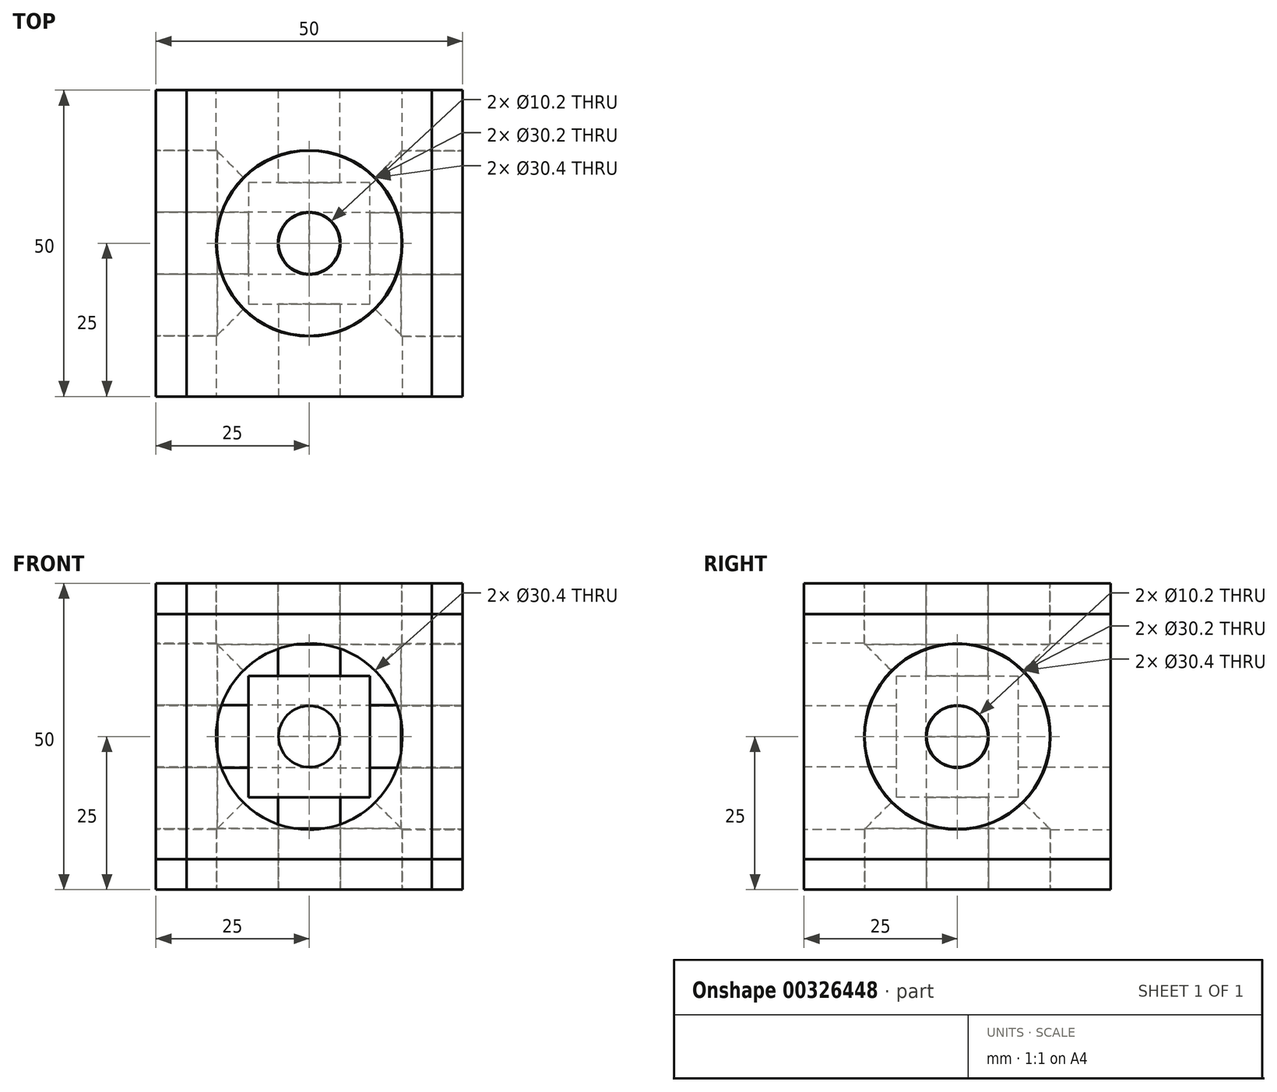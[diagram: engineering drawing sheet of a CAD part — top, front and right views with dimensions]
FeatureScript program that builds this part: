
annotation { "Feature Type Name" : "Feature", "Feature Type Description" : "" }
export const myFeature = defineFeature(function(context is Context, id is Id, definition is map)
    precondition{}
    {
        {
            var Q0;
            Q0=qCreatedBy(makeId("Top.planeOp"),FACE);
            var sketch = newSketch(context, id + "F0", { "sketchPlane" : qUnion([Q0])});
            skLineSegment(sketch, "E0.bottom", {"start": v(25, -25) * mm, "end": v(-25, -25) * mm});
            skLineSegment(sketch, "E0.top", {"start": v(25, 25) * mm, "end": v(-25, 25) * mm});
            skLineSegment(sketch, "E0.left", {"start": v(25, -25) * mm, "end": v(25, 25) * mm});
            skLineSegment(sketch, "E0.right", {"start": v(-25, -25) * mm, "end": v(-25, 25) * mm});
            skPoint(sketch, "E0.middle", {"position": v(0, 0) * mm});
            skSolve(sketch);
        }
        {
            var Q0;
            Q0 = qSketchRegion(id + "F0", true);
            extrude(context, id + "F1", {"entities" : qUnion([Q0]), "endBound" : BoundingType.SYMMETRIC, "depth" : 50 * mm});
        }
        {
            var Q0;
            Q0=makeQuery(id+"F1.opExtrude","CAP_FACE",FACE,{"disambiguationData":[OSD([sQuery(id+"F0.wireOp",EDGE,"E0.bottom"),sQuery(id+"F0.wireOp",EDGE,"E0.top"),sQuery(id+"F0.wireOp",EDGE,"E0.left"),sQuery(id+"F0.wireOp",EDGE,"E0.right")])],"isStart":false});
            var sketch = newSketch(context, id + "F2", { "sketchPlane" : qUnion([Q0])});
            skCircle(sketch, "E1", {"center": v(0, 0) * mm, "radius": 15.1 * mm});
            skCircle(sketch, "E2", {"center": v(0, 0) * mm, "radius": 5.1 * mm});
            skSolve(sketch);
        }
        {
            var Q0;
            Q0=qCreatedBy(makeId("Top.planeOp"),FACE);
            var sketch = newSketch(context, id + "F3", { "sketchPlane" : qUnion([Q0])});
            skPoint(sketch, "E3.0", {"position": v(0, 25) * mm});
            skPoint(sketch, "E4.0", {"position": v(0, -25) * mm});
            skLineSegment(sketch, "E5", {"start": v(0, 25) * mm, "end": v(0, -25) * mm, "construction": true});
            skPoint(sketch, "E6.0", {"position": v(-25, 0) * mm});
            skPoint(sketch, "E7.0", {"position": v(25, 0) * mm});
            skLineSegment(sketch, "E8", {"start": v(-25, 0) * mm, "end": v(25, 0) * mm, "construction": true});
            skSolve(sketch);
        }
        {
            var Q0;
            Q0=makeQuery(id+"F2.imprint","IMPRINT",FACE,{"disambiguationData":[TD([[makeQuery(id+"F2.imprint","IMPRINT",EDGE,{"derivedFrom":sQuery(id+"F2.wireOp",EDGE,"E2")}),1.0]])]});
            extrude(context, id + "F4", {"entities" : qUnion([Q0]), "oppositeDirection" : true, "depth" : 25 * mm});
        }
        {
            var Q0;
            Q0=makeQuery(id+"F2.imprint","IMPRINT",FACE,{"disambiguationData":[TD([[makeQuery(id+"F2.imprint","IMPRINT",EDGE,{"derivedFrom":sQuery(id+"F2.wireOp",EDGE,"E1")}),1.0]])]});
            extrude(context, id + "F5", {"entities" : qUnion([Q0]), "oppositeDirection" : true, "depth" : 15 * mm});
        }
        {
            var Q0;
            Q0=makeQuery(id+"F2.imprint","IMPRINT",FACE,{"disambiguationData":[TD([[makeQuery(id+"F2.imprint","IMPRINT",EDGE,{"derivedFrom":sQuery(id+"F2.wireOp",EDGE,"E1")}),1.0]])]});
            extrude(context, id + "F6", {"entities" : qUnion([Q0]), "oppositeDirection" : true, "depth" : 10 * mm});
        }
        {
            var Q0;
            Q0=makeQuery(id+"F2.imprint","IMPRINT",FACE,{"disambiguationData":[TD([[makeQuery(id+"F2.imprint","IMPRINT",EDGE,{"derivedFrom":sQuery(id+"F2.wireOp",EDGE,"E1")}),-1.0]])]});
            extrude(context, id + "F7", {"entities" : qUnion([Q0]), "oppositeDirection" : true, "depth" : 5 * mm});
        }
        {
            var Q0;
            Q0=makeQuery(id+"F4.opExtrude","SWEPT_BODY",BODY,{"disambiguationData":[OSD([sQuery(id+"F2.wireOp",EDGE,"E2")])]});
            var Q1;
            Q1=makeQuery(id+"F5.opExtrude","SWEPT_BODY",BODY,{"disambiguationData":[OSD([sQuery(id+"F2.wireOp",EDGE,"O8aLxC34-7BVB-v1Gc-gPhH-KugDPPAYjpQ1"),sQuery(id+"F2.wireOp",EDGE,"E2")])]});
            var Q2;
            Q2=makeQuery(id+"F6.opExtrude","SWEPT_BODY",BODY,{"disambiguationData":[OSD([sQuery(id+"F2.wireOp",EDGE,"E1"),sQuery(id+"F2.wireOp",EDGE,"O8aLxC34-7BVB-v1Gc-gPhH-KugDPPAYjpQ1")])]});
            var Q3;
            Q3=makeQuery(id+"F7.opExtrude","SWEPT_BODY",BODY,{"disambiguationData":[OSD([sQuery(id+"F2.wireOp",EDGE,"E1"),sQuery(id+"F2.wireOp",EDGE,"bVq9zxu4-4mFd-veg9-z9kG-BxlB4XuhqD94")])]});
            var Q4;
            Q4=sQuery(id+"F3.wireOp",EDGE,"E5");
            circularPattern(context, id + "F8", {"entities" : qUnion([Q0, Q1, Q2, Q3]), "axis" : qUnion([Q4]), "angle" : 360 * degree, "instanceCount" : 4, "equalSpace" : true});
        }
        {
            var Q0;
            Q0=makeQuery(id+"F5.opExtrude","SWEPT_BODY",BODY,{"disambiguationData":[OSD([sQuery(id+"F2.wireOp",EDGE,"O8aLxC34-7BVB-v1Gc-gPhH-KugDPPAYjpQ1"),sQuery(id+"F2.wireOp",EDGE,"E2")])]});
            var Q1;
            Q1=sQuery(id+"F3.wireOp",EDGE,"E8");
            circularPattern(context, id + "F9", {"entities" : qUnion([Q0]), "axis" : qUnion([Q1]), "angle" : 360 * degree, "instanceCount" : 4, "equalSpace" : true});
        }
        {
            var Q0;
            Q0=makeQuery(id+"F9.opPattern","COPY",BODY,{"derivedFrom":makeQuery(id+"F5.opExtrude","SWEPT_BODY",BODY,{"disambiguationData":[OSD([sQuery(id+"F2.wireOp",EDGE,"O8aLxC34-7BVB-v1Gc-gPhH-KugDPPAYjpQ1"),sQuery(id+"F2.wireOp",EDGE,"E2")])]}),"instanceName":"2"});
            deleteBodies(context, id + "F10", {"entities" : qUnion([Q0])});
        }
        {
            var Q0;
            Q0=makeQuery(id+"F5.opExtrude","SWEPT_BODY",BODY,{"disambiguationData":[OSD([sQuery(id+"F2.wireOp",EDGE,"O8aLxC34-7BVB-v1Gc-gPhH-KugDPPAYjpQ1"),sQuery(id+"F2.wireOp",EDGE,"E2")])]});
            var Q1;
            Q1=makeQuery(id+"F8.opPattern","COPY",BODY,{"derivedFrom":makeQuery(id+"F5.opExtrude","SWEPT_BODY",BODY,{"disambiguationData":[OSD([sQuery(id+"F2.wireOp",EDGE,"O8aLxC34-7BVB-v1Gc-gPhH-KugDPPAYjpQ1"),sQuery(id+"F2.wireOp",EDGE,"E2")])]}),"instanceName":"1"});
            var Q2;
            Q2=makeQuery(id+"F8.opPattern","COPY",BODY,{"derivedFrom":makeQuery(id+"F5.opExtrude","SWEPT_BODY",BODY,{"disambiguationData":[OSD([sQuery(id+"F2.wireOp",EDGE,"O8aLxC34-7BVB-v1Gc-gPhH-KugDPPAYjpQ1"),sQuery(id+"F2.wireOp",EDGE,"E2")])]}),"instanceName":"2"});
            var Q3;
            Q3=makeQuery(id+"F8.opPattern","COPY",BODY,{"derivedFrom":makeQuery(id+"F5.opExtrude","SWEPT_BODY",BODY,{"disambiguationData":[OSD([sQuery(id+"F2.wireOp",EDGE,"O8aLxC34-7BVB-v1Gc-gPhH-KugDPPAYjpQ1"),sQuery(id+"F2.wireOp",EDGE,"E2")])]}),"instanceName":"3"});
            var Q4;
            Q4=makeQuery(id+"F9.opPattern","COPY",BODY,{"derivedFrom":makeQuery(id+"F5.opExtrude","SWEPT_BODY",BODY,{"disambiguationData":[OSD([sQuery(id+"F2.wireOp",EDGE,"O8aLxC34-7BVB-v1Gc-gPhH-KugDPPAYjpQ1"),sQuery(id+"F2.wireOp",EDGE,"E2")])]}),"instanceName":"1"});
            var Q5;
            Q5=makeQuery(id+"F9.opPattern","COPY",BODY,{"derivedFrom":makeQuery(id+"F5.opExtrude","SWEPT_BODY",BODY,{"disambiguationData":[OSD([sQuery(id+"F2.wireOp",EDGE,"O8aLxC34-7BVB-v1Gc-gPhH-KugDPPAYjpQ1"),sQuery(id+"F2.wireOp",EDGE,"E2")])]}),"instanceName":"3"});
            var Q6;
            Q6=makeQuery(id+"F1.opExtrude","SWEPT_BODY",BODY,{"disambiguationData":[OSD([sQuery(id+"F0.wireOp",EDGE,"E0.bottom"),sQuery(id+"F0.wireOp",EDGE,"E0.top"),sQuery(id+"F0.wireOp",EDGE,"E0.left"),sQuery(id+"F0.wireOp",EDGE,"E0.right")])]});
            booleanBodies(context, id + "F11", {"operationType" : BooleanOperationType.SUBTRACTION, "tools" : qUnion([Q0, Q1, Q2, Q3, Q4, Q5]), "targets" : qUnion([Q6]), "offset" : true, "offsetAll" : true, "offsetDistance" : .1 * mm});
        }
    });
